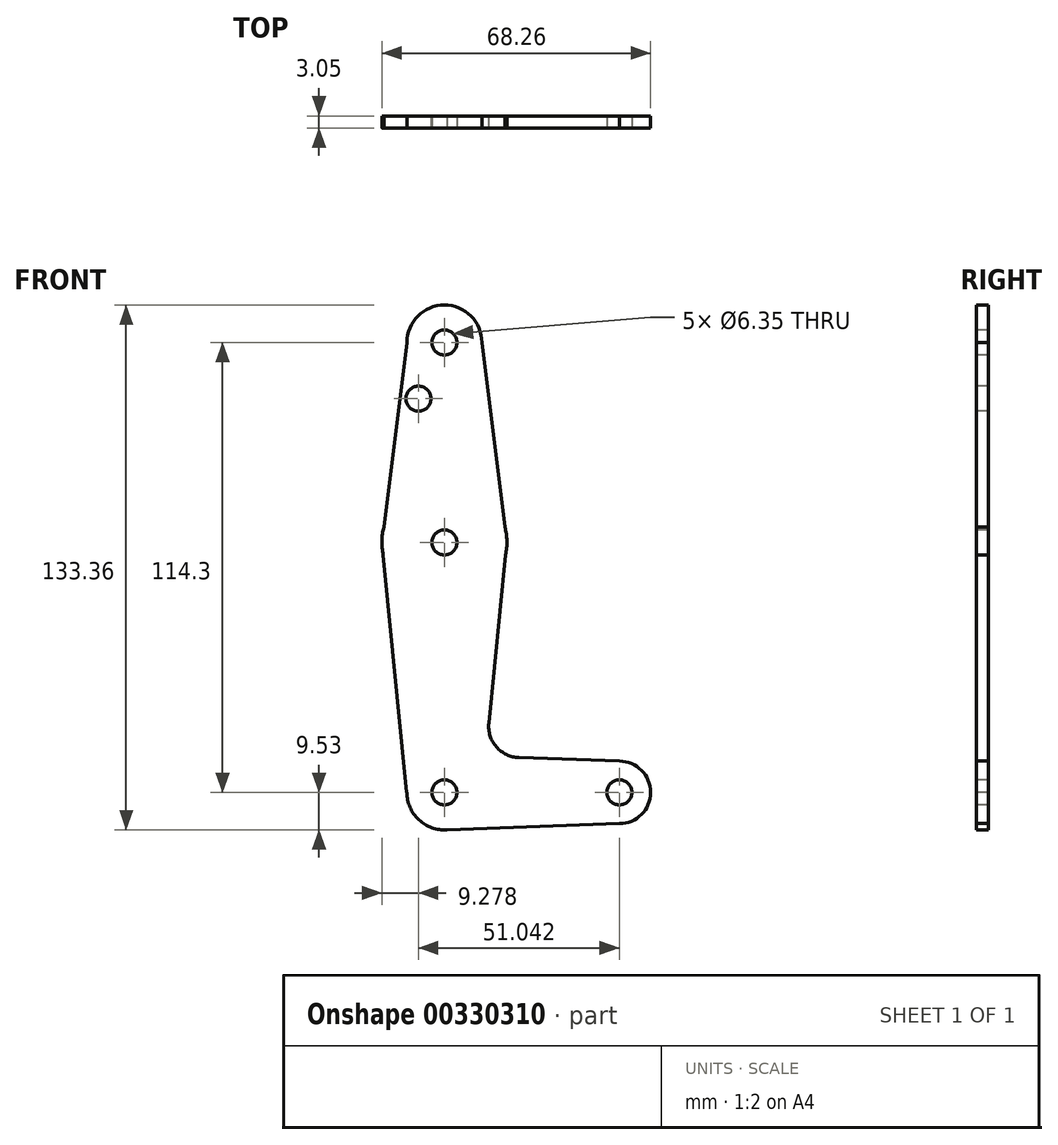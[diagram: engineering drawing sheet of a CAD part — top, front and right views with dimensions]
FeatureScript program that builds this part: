
annotation { "Feature Type Name" : "Feature", "Feature Type Description" : "" }
export const myFeature = defineFeature(function(context is Context, id is Id, definition is map)
    precondition{}
    {
        {
            var Q0;
            Q0=qCreatedBy(makeId("Front.planeOp"),FACE);
            var sketch = newSketch(context, id + "F0", { "sketchPlane" : qUnion([Q0])});
            skCircle(sketch, "E0", {"center": v(0, 0) * mm, "radius": 9.53 * mm});
            skCircle(sketch, "E1", {"center": v(44.45, 0) * mm, "radius": 7.94 * mm});
            skCircle(sketch, "E2", {"center": v(0, 63.5) * mm, "radius": 15.88 * mm});
            skCircle(sketch, "E3", {"center": v(0, 114.3) * mm, "radius": 9.53 * mm});
            skLineSegment(sketch, "E4", {"start": v(0, 114.3) * mm, "end": v(0, 0) * mm});
            skLineSegment(sketch, "E5", {"start": v(44.45, 0) * mm, "end": v(0, 0) * mm});
            skLineSegment(sketch, "E6", {"start": v(-9.53, 114.3) * mm, "end": v(-15.88, 63.5) * mm});
            skLineSegment(sketch, "E7", {"start": v(9.52, 114.3) * mm, "end": v(15.88, 63.5) * mm});
            skLineSegment(sketch, "E8", {"start": v(-15.88, 63.5) * mm, "end": v(-9.57, 0) * mm});
            skLineSegment(sketch, "E9", {"start": v(15.88, 63.5) * mm, "end": v(11.28, 17.59) * mm});
            skLineSegment(sketch, "E10", {"start": v(18.91, 8.85) * mm, "end": v(44.45, 7.94) * mm});
            skLineSegment(sketch, "E11", {"start": v(44.45, -7.94) * mm, "end": v(0, -9.52) * mm});
            skCircle(sketch, "E12", {"center": v(0, 114.3) * mm, "radius": 3.18 * mm});
            skCircle(sketch, "E13", {"center": v(0, 63.5) * mm, "radius": 3.18 * mm});
            skCircle(sketch, "E14", {"center": v(0, 0) * mm, "radius": 3.18 * mm});
            skCircle(sketch, "E15", {"center": v(44.45, 0) * mm, "radius": 3.18 * mm});
            skCircle(sketch, "E16", {"center": v(-6.6, 100.03) * mm, "radius": 3.18 * mm});
            skArc(sketch, "E17.filletArc", {"start": v(11.28, 17.59) * mm, "mid": v(13.2, 11.57) * mm, "end": v(18.91, 8.85) * mm});
            skLineSegment(sketch, "E18", {"start": v(-9.57, 0) * mm, "end": v(-9.53, 0) * mm});
            skSolve(sketch);
        }
        {
            var Q0;
            {var subQ0=sQuery(id+"F0.wireOp",EDGE,"E11");var subQ1=sQuery(id+"F0.wireOp",EDGE,"E0");var subQ2=makeQuery(id+"F0.imprint","INTERSECT",VERTEX,{"disambiguationData":[OD(0.0)],"derivedFrom":[subQ1,subQ0]});Q0=makeQuery(id+"F0.imprint","IMPRINT",FACE,{"disambiguationData":[TD([[makeQuery(id+"F0.imprint","IMPRINT",EDGE,{"disambiguationData":[TD([[subQ2,-1.0]])],"derivedFrom":subQ1}),1.0]])]});}
            var Q1;
            {var subQ0=sQuery(id+"F0.wireOp",EDGE,"E7");var subQ1=sQuery(id+"F0.wireOp",EDGE,"E2");var subQ3=makeQuery(id+"F0.imprint","INTERSECT",VERTEX,{"derivedFrom":[subQ1,subQ0]});Q1=makeQuery(id+"F0.imprint","IMPRINT",FACE,{"disambiguationData":[TD([[makeQuery(id+"F0.imprint","IMPRINT",EDGE,{"disambiguationData":[TD([[subQ3,1.0]])],"derivedFrom":subQ1}),1.0]])]});}
            var Q2;
            {var subQ0=sQuery(id+"F0.wireOp",EDGE,"E6");var subQ1=sQuery(id+"F0.wireOp",EDGE,"E2");var subQ3=makeQuery(id+"F0.imprint","INTERSECT",VERTEX,{"derivedFrom":[subQ1,subQ0]});Q2=makeQuery(id+"F0.imprint","IMPRINT",FACE,{"disambiguationData":[TD([[makeQuery(id+"F0.imprint","IMPRINT",EDGE,{"disambiguationData":[TD([[subQ3,-1.0]])],"derivedFrom":subQ1}),1.0]])]});}
            var Q3;
            {var subQ0=sQuery(id+"F0.wireOp",EDGE,"E8");var subQ1=sQuery(id+"F0.wireOp",EDGE,"E2");var subQ3=makeQuery(id+"F0.imprint","INTERSECT",VERTEX,{"derivedFrom":[subQ1,subQ0]});Q3=makeQuery(id+"F0.imprint","IMPRINT",FACE,{"disambiguationData":[TD([[makeQuery(id+"F0.imprint","IMPRINT",EDGE,{"disambiguationData":[TD([[subQ3,1.0]])],"derivedFrom":subQ1}),1.0]])]});}
            var Q4;
            {var subQ0=sQuery(id+"F0.wireOp",EDGE,"E9");var subQ1=sQuery(id+"F0.wireOp",EDGE,"E2");var subQ3=makeQuery(id+"F0.imprint","INTERSECT",VERTEX,{"derivedFrom":[subQ1,subQ0]});Q4=makeQuery(id+"F0.imprint","IMPRINT",FACE,{"disambiguationData":[TD([[makeQuery(id+"F0.imprint","IMPRINT",EDGE,{"disambiguationData":[TD([[subQ3,-1.0]])],"derivedFrom":subQ1}),1.0]])]});}
            var Q5;
            {var subQ0=sQuery(id+"F0.wireOp",EDGE,"E18");Q5=makeQuery(id+"F0.imprint","IMPRINT",FACE,{"disambiguationData":[TD([[makeQuery(id+"F0.imprint","IMPRINT",EDGE,{"derivedFrom":subQ0}),1.0]])]});}
            var Q6;
            {var subQ0=sQuery(id+"F0.wireOp",EDGE,"E11");var subQ1=sQuery(id+"F0.wireOp",EDGE,"E0");var subQ2=makeQuery(id+"F0.imprint","INTERSECT",VERTEX,{"disambiguationData":[OD(1.0)],"derivedFrom":[subQ1,subQ0]});Q6=makeQuery(id+"F0.imprint","IMPRINT",FACE,{"disambiguationData":[TD([[makeQuery(id+"F0.imprint","IMPRINT",EDGE,{"disambiguationData":[TD([[subQ2,-1.0]])],"derivedFrom":subQ1}),-1.0]])]});}
            var Q7;
            Q7=makeQuery(id+"F0.imprint","IMPRINT",FACE,{"disambiguationData":[TD([[makeQuery(id+"F0.imprint","IMPRINT",EDGE,{"derivedFrom":sQuery(id+"F0.wireOp",EDGE,"E15")}),-1.0]])]});
            var Q8;
            {var subQ0=sQuery(id+"F0.wireOp",EDGE,"E4");var subQ1=sQuery(id+"F0.wireOp",EDGE,"E0");var subQ2=makeQuery(id+"F0.imprint","INTERSECT",VERTEX,{"derivedFrom":[subQ1,subQ0]});Q8=makeQuery(id+"F0.imprint","IMPRINT",FACE,{"disambiguationData":[TD([[makeQuery(id+"F0.imprint","IMPRINT",EDGE,{"disambiguationData":[TD([[subQ2,1.0]])],"derivedFrom":subQ1}),1.0]])]});}
            var Q9;
            {var subQ1=sQuery(id+"F0.wireOp",EDGE,"E2");var subQ7=sQuery(id+"F0.wireOp",EDGE,"E7");var subQ8=makeQuery(id+"F0.imprint","INTERSECT",VERTEX,{"derivedFrom":[subQ1,subQ7]});Q9=makeQuery(id+"F0.imprint","IMPRINT",FACE,{"disambiguationData":[TD([[makeQuery(id+"F0.imprint","IMPRINT",EDGE,{"disambiguationData":[TD([[subQ8,-1.0]])],"derivedFrom":subQ1}),1.0]])]});}
            var Q10;
            {var subQ0=sQuery(id+"F0.wireOp",EDGE,"E7");var subQ1=sQuery(id+"F0.wireOp",EDGE,"E2");var subQ2=makeQuery(id+"F0.imprint","INTERSECT",VERTEX,{"derivedFrom":[subQ1,subQ0]});Q10=makeQuery(id+"F0.imprint","IMPRINT",FACE,{"disambiguationData":[TD([[makeQuery(id+"F0.imprint","IMPRINT",EDGE,{"disambiguationData":[TD([[subQ2,-1.0]])],"derivedFrom":subQ1}),-1.0]])]});}
            var Q11;
            Q11=makeQuery(id+"F0.imprint","IMPRINT",FACE,{"disambiguationData":[TD([[makeQuery(id+"F0.imprint","IMPRINT",EDGE,{"derivedFrom":sQuery(id+"F0.wireOp",EDGE,"E16")}),-1.0]])]});
            var Q12;
            {var subQ8=sQuery(id+"F0.wireOp",EDGE,"E10");Q12=makeQuery(id+"F0.imprint","IMPRINT",FACE,{"disambiguationData":[TD([[makeQuery(id+"F0.imprint","IMPRINT",EDGE,{"derivedFrom":subQ8}),-1.0]])]});}
            var Q13;
            {var subQ1=sQuery(id+"F0.wireOp",EDGE,"E2");var subQ6=sQuery(id+"F0.wireOp",EDGE,"E6");var subQ11=makeQuery(id+"F0.imprint","INTERSECT",VERTEX,{"derivedFrom":[subQ1,subQ6]});Q13=makeQuery(id+"F0.imprint","IMPRINT",FACE,{"disambiguationData":[TD([[makeQuery(id+"F0.imprint","IMPRINT",EDGE,{"disambiguationData":[TD([[subQ11,1.0]])],"derivedFrom":subQ1}),1.0]])]});}
            var Q14;
            Q14=makeQuery(id+"F0.imprint","IMPRINT",FACE,{"disambiguationData":[TD([[makeQuery(id+"F0.imprint","IMPRINT",EDGE,{"derivedFrom":sQuery(id+"F0.wireOp",EDGE,"E12")}),-1.0]])]});
            var Q15;
            {var subQ1=sQuery(id+"F0.wireOp",EDGE,"E0");var subQ7=makeQuery(id+"F0.imprint","INTERSECT",VERTEX,{"derivedFrom":[subQ1,sQuery(id+"F0.wireOp",EDGE,"E18")]});Q15=makeQuery(id+"F0.imprint","IMPRINT",FACE,{"disambiguationData":[TD([[makeQuery(id+"F0.imprint","IMPRINT",EDGE,{"disambiguationData":[TD([[subQ7,1.0]])],"derivedFrom":subQ1}),1.0]])]});}
            extrude(context, id + "F1", {"entities" : qUnion([Q0, Q1, Q2, Q3, Q4, Q5, Q6, Q7, Q8, Q9, Q10, Q11, Q12, Q13, Q14, Q15]), "oppositeDirection" : true, "depth" : 3.05 * mm});
        }
    });
